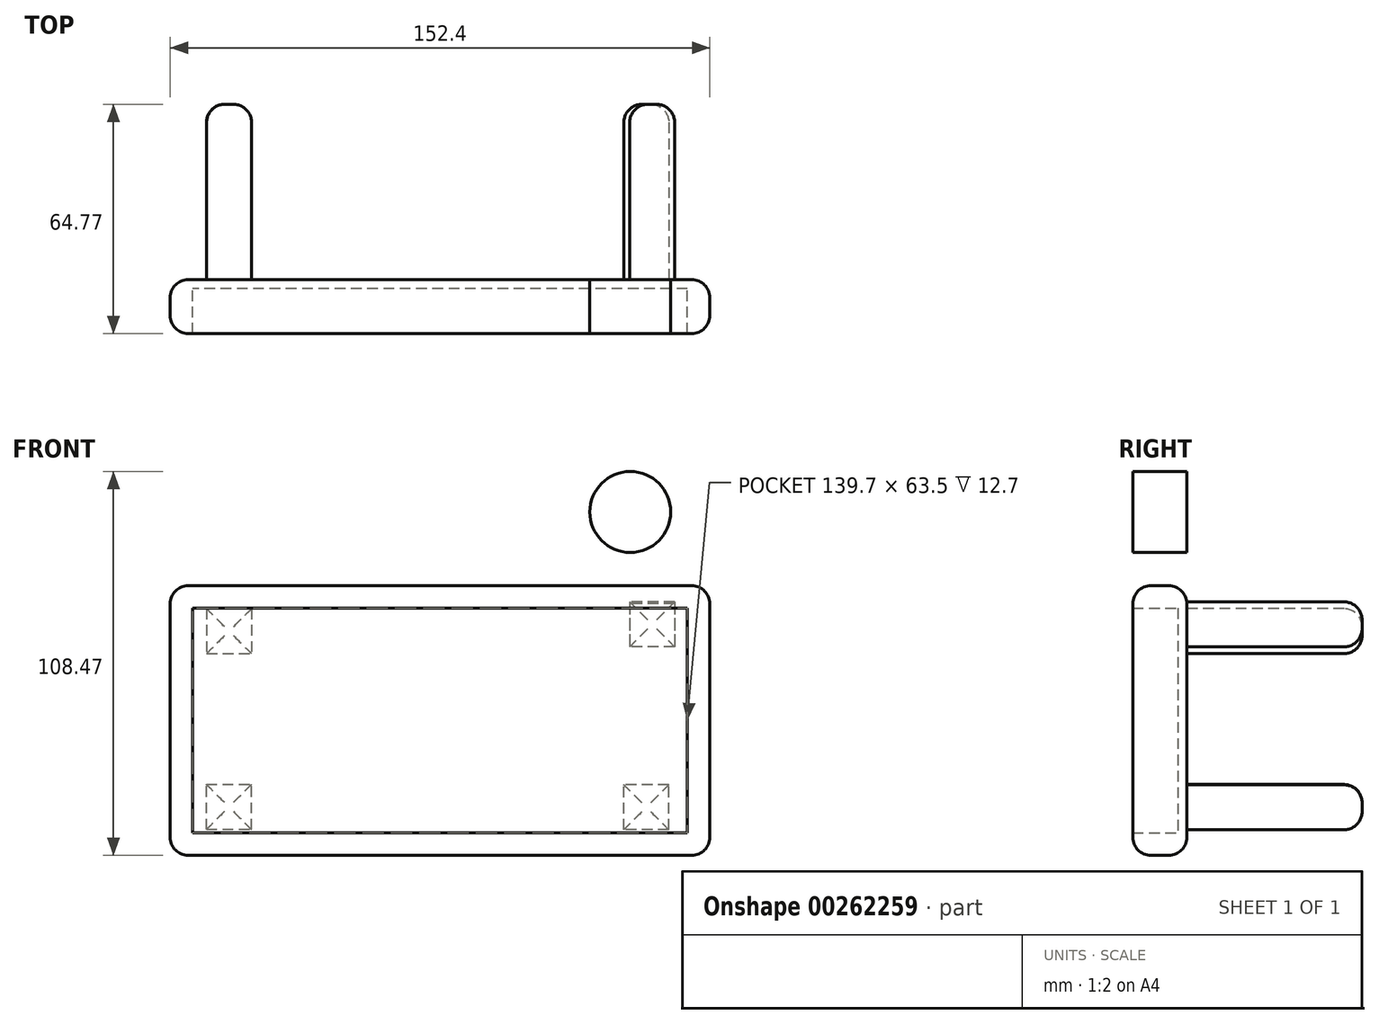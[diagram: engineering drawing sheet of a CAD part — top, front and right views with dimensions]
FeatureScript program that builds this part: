
annotation { "Feature Type Name" : "Feature", "Feature Type Description" : "" }
export const myFeature = defineFeature(function(context is Context, id is Id, definition is map)
    precondition{}
    {
        {
            var Q0;
            Q0=qCreatedBy(makeId("Front.planeOp"),FACE);
            var sketch = newSketch(context, id + "F0", { "sketchPlane" : qUnion([Q0])});
            skLineSegment(sketch, "E0.bottom", {"start": v(76.2, 40.62) * mm, "end": v(-76.2, 40.62) * mm});
            skLineSegment(sketch, "E0.top", {"start": v(76.2, -35.58) * mm, "end": v(-76.2, -35.58) * mm});
            skLineSegment(sketch, "E0.left", {"start": v(76.2, 40.62) * mm, "end": v(76.2, -35.58) * mm});
            skLineSegment(sketch, "E0.right", {"start": v(-76.2, 40.62) * mm, "end": v(-76.2, -35.58) * mm});
            skPoint(sketch, "E0.middle", {"position": v(0, 2.52) * mm});
            skLineSegment(sketch, "E1.bottom", {"start": v(69.85, 34.27) * mm, "end": v(-69.85, 34.27) * mm});
            skLineSegment(sketch, "E1.top", {"start": v(69.85, -29.23) * mm, "end": v(-69.85, -29.23) * mm});
            skLineSegment(sketch, "E1.left", {"start": v(69.85, 34.27) * mm, "end": v(69.85, -29.23) * mm});
            skLineSegment(sketch, "E1.right", {"start": v(-69.85, 34.27) * mm, "end": v(-69.85, -29.23) * mm});
            skLineSegment(sketch, "E2.left", {"start": v(69.85, -29.23) * mm, "end": v(69.85, 34.27) * mm});
            skPoint(sketch, "E3.middle", {"position": v(-69.85, 34.27) * mm});
            skCircle(sketch, "E4", {"center": v(53.73, 61.46) * mm, "radius": 11.43 * mm});
            skSolve(sketch);
        }
        {
            var Q0;
            Q0 = qSketchRegion(id + "F0", true);
            extrude(context, id + "F1", {"entities" : qUnion([Q0]), "depth" : 15.24 * mm});
        }
        {
            var Q0;
            Q0=makeQuery(id+"F0.imprint","IMPRINT",FACE,{"disambiguationData":[TD([[makeQuery(id+"F0.imprint","IMPRINT",EDGE,{"derivedFrom":sQuery(id+"F0.wireOp",EDGE,"E1.right")}),1.0]])]});
            var Q1;
            {var subQ7=sQuery(id+"F0.wireOp",EDGE,"iMsUwTD6-5xW9-ojue-fTqp-QAsr3j2GOEwt");var subQ13=sQuery(id+"F0.wireOp",EDGE,"E1.right");var subQ14=makeQuery(id+"F0.imprint","INTERSECT",VERTEX,{"derivedFrom":[subQ13,subQ7]});Q1=makeQuery(id+"F0.imprint","IMPRINT",FACE,{"disambiguationData":[TD([[makeQuery(id+"F0.imprint","IMPRINT",EDGE,{"disambiguationData":[TD([[subQ14,-1.0]])],"derivedFrom":subQ13}),1.0]])]});}
            extrude(context, id + "F2", {"entities" : qUnion([Q0, Q1]), "operationType" : NewBodyOperationType.ADD, "depth" : 2.54 * mm});
        }
        {
            var Q0;
            Q0=makeQuery(id+"F1.opExtrude","CAP_EDGE",EDGE,{"disambiguationData":[OSD([sQuery(id+"F0.wireOp",EDGE,"E0.right")])],"isStart":false});
            var Q1;
            Q1=makeQuery(id+"F1.opExtrude","CAP_EDGE",EDGE,{"disambiguationData":[OSD([sQuery(id+"F0.wireOp",EDGE,"E0.left")])],"isStart":false});
            var Q2;
            Q2=makeQuery(id+"F1.opExtrude","SWEPT_FACE",FACE,{"disambiguationData":[OSD([sQuery(id+"F0.wireOp",EDGE,"E0.top")])]});
            var Q3;
            Q3=makeQuery(id+"F1.opExtrude","SWEPT_FACE",FACE,{"disambiguationData":[OSD([sQuery(id+"F0.wireOp",EDGE,"E0.left")])]});
            var Q4;
            Q4=makeQuery(id+"F1.opExtrude","SWEPT_FACE",FACE,{"disambiguationData":[OSD([sQuery(id+"F0.wireOp",EDGE,"E0.right")])]});
            var Q5;
            Q5=makeQuery(id+"F1.opExtrude","SWEPT_FACE",FACE,{"disambiguationData":[OSD([sQuery(id+"F0.wireOp",EDGE,"E0.bottom")])]});
            fillet(context, id + "F3", {"entities" : qUnion([Q0, Q1, Q2, Q3, Q4, Q5]), "radius" : 5.08 * mm, "tangentPropagation" : true, "allowEdgeOverflow" : false});
        }
        {
            var Q0;
            Q0=qCreatedBy(makeId("Front.planeOp"),FACE);
            var sketch = newSketch(context, id + "F4", { "sketchPlane" : qUnion([Q0])});
            skLineSegment(sketch, "E5.bottom", {"start": v(66.26, 36.06) * mm, "end": v(53.56, 36.06) * mm});
            skLineSegment(sketch, "E5.top", {"start": v(66.26, 23.36) * mm, "end": v(53.56, 23.36) * mm});
            skLineSegment(sketch, "E5.left", {"start": v(66.26, 36.06) * mm, "end": v(66.26, 23.36) * mm});
            skLineSegment(sketch, "E5.right", {"start": v(53.56, 36.06) * mm, "end": v(53.56, 23.36) * mm});
            skLineSegment(sketch, "E6.bottom", {"start": v(64.6, -28.34) * mm, "end": v(51.9, -28.34) * mm});
            skLineSegment(sketch, "E6.top", {"start": v(64.6, -15.64) * mm, "end": v(51.9, -15.64) * mm});
            skLineSegment(sketch, "E6.left", {"start": v(64.6, -28.34) * mm, "end": v(64.6, -15.64) * mm});
            skLineSegment(sketch, "E6.right", {"start": v(51.9, -28.34) * mm, "end": v(51.9, -15.64) * mm});
            skLineSegment(sketch, "E7.bottom", {"start": v(-65.93, 34.13) * mm, "end": v(-53.23, 34.13) * mm});
            skLineSegment(sketch, "E7.top", {"start": v(-65.93, 21.43) * mm, "end": v(-53.23, 21.43) * mm});
            skLineSegment(sketch, "E7.left", {"start": v(-65.93, 34.13) * mm, "end": v(-65.93, 21.43) * mm});
            skLineSegment(sketch, "E7.right", {"start": v(-53.23, 34.13) * mm, "end": v(-53.23, 21.43) * mm});
            skLineSegment(sketch, "E8.bottom", {"start": v(-65.98, -28.26) * mm, "end": v(-53.28, -28.26) * mm});
            skLineSegment(sketch, "E8.top", {"start": v(-65.98, -15.56) * mm, "end": v(-53.28, -15.56) * mm});
            skLineSegment(sketch, "E8.left", {"start": v(-65.98, -28.26) * mm, "end": v(-65.98, -15.56) * mm});
            skLineSegment(sketch, "E8.right", {"start": v(-53.28, -28.26) * mm, "end": v(-53.28, -15.56) * mm});
            skSolve(sketch);
        }
        {
            var Q0;
            Q0=makeQuery(id+"F4.imprint","IMPRINT",FACE,{"disambiguationData":[TD([[makeQuery(id+"F4.imprint","IMPRINT",EDGE,{"derivedFrom":sQuery(id+"F4.wireOp",EDGE,"E5.bottom")}),1.0]])]});
            var Q1;
            Q1=makeQuery(id+"F4.imprint","IMPRINT",FACE,{"disambiguationData":[TD([[makeQuery(id+"F4.imprint","IMPRINT",EDGE,{"derivedFrom":sQuery(id+"F4.wireOp",EDGE,"E6.bottom")}),-1.0]])]});
            var Q2;
            Q2=makeQuery(id+"F4.imprint","IMPRINT",FACE,{"disambiguationData":[TD([[makeQuery(id+"F4.imprint","IMPRINT",EDGE,{"derivedFrom":sQuery(id+"F4.wireOp",EDGE,"E8.bottom")}),1.0]])]});
            var Q3;
            Q3=makeQuery(id+"F4.imprint","IMPRINT",FACE,{"disambiguationData":[TD([[makeQuery(id+"F4.imprint","IMPRINT",EDGE,{"derivedFrom":sQuery(id+"F4.wireOp",EDGE,"E7.bottom")}),-1.0]])]});
            extrude(context, id + "F5", {"entities" : qUnion([Q0, Q1, Q2, Q3]), "operationType" : NewBodyOperationType.ADD, "oppositeDirection" : true, "depth" : 49.53 * mm});
        }
        {
            var Q0;
            Q0=makeQuery(id+"F5.opExtrude","CAP_FACE",FACE,{"disambiguationData":[OSD([sQuery(id+"F4.wireOp",EDGE,"E6.bottom"),sQuery(id+"F4.wireOp",EDGE,"E6.top"),sQuery(id+"F4.wireOp",EDGE,"E6.left"),sQuery(id+"F4.wireOp",EDGE,"E6.right")])],"isStart":false});
            var Q1;
            Q1=makeQuery(id+"F5.opExtrude","CAP_FACE",FACE,{"disambiguationData":[OSD([sQuery(id+"F4.wireOp",EDGE,"E8.bottom"),sQuery(id+"F4.wireOp",EDGE,"E8.top"),sQuery(id+"F4.wireOp",EDGE,"E8.left"),sQuery(id+"F4.wireOp",EDGE,"E8.right")])],"isStart":false});
            var Q2;
            Q2=makeQuery(id+"F5.opExtrude","CAP_FACE",FACE,{"disambiguationData":[OSD([sQuery(id+"F4.wireOp",EDGE,"E5.bottom"),sQuery(id+"F4.wireOp",EDGE,"E5.top"),sQuery(id+"F4.wireOp",EDGE,"E5.left"),sQuery(id+"F4.wireOp",EDGE,"E5.right")])],"isStart":false});
            var Q3;
            Q3=makeQuery(id+"F5.opExtrude","CAP_FACE",FACE,{"disambiguationData":[OSD([sQuery(id+"F4.wireOp",EDGE,"E7.bottom"),sQuery(id+"F4.wireOp",EDGE,"E7.top"),sQuery(id+"F4.wireOp",EDGE,"E7.left"),sQuery(id+"F4.wireOp",EDGE,"E7.right")])],"isStart":false});
            fillet(context, id + "F6", {"entities" : qUnion([Q0, Q1, Q2, Q3]), "radius" : 5.08 * mm, "tangentPropagation" : true, "allowEdgeOverflow" : false});
        }
    });
